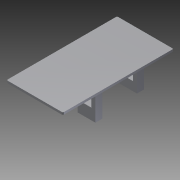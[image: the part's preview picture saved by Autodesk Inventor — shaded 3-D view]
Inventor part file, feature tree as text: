
AUTODESK INVENTOR PART (.ipt)
format: ipt  version: 2014 (Build 180170000, 170)  size: 112,640 bytes
history: native  units: in
note: dims shown in document units (in); Inventor stores cm internally (conversion verified against a paired STEP export)
features: other x7, extrude x3, sketch x3
ambient origin geometry x8: Origin, YZ Plane, XZ Plane, XY Plane, X Axis, Y Axis, Z Axis, Center Point
bodies: Solid1 (feature_tree)
feature tree (13):
  extrude  "Extrusion1"  Depth=0.031in TaperAngle=0.0deg
  extrude  "Extrusion2"  [1 undecoded]
  extrude  "Extrusion3"  [1 undecoded]
  other  "to_base_XY"
  other  "to_base_YZ"
  other  "to_base_ZX"
  other  "to_base_X"
  other  "to_base_Y"
  other  "to_base_Z"
  other  "to_base_Center"
  sketch  "Sketch_2"  dims[d0=0.01in d1=0.0in d2=0.031in d3=0.0in]
  sketch  "Sketch_12"  dims[d4=0.031in d5=0.0in]
  sketch  "Sketch_14"
note: 2 required parameter values undecoded (feature->parameter linkage not recoverable at this tier; creation-order binding heuristic only, values carry confidence <= 0.55)
